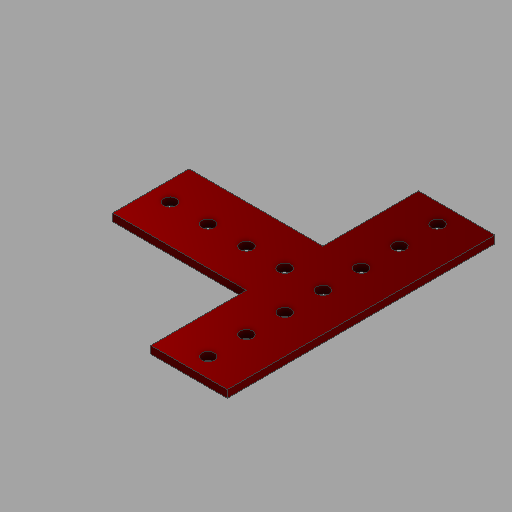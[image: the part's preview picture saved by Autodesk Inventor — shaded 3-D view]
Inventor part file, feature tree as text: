
AUTODESK INVENTOR PART (.ipt)
format: ipt  version: 2024.2 (Build 282272000, 272)  size: 332,800 bytes
history: native  units: in
note: dims shown in document units (in); Inventor stores cm internally (conversion verified against a paired STEP export)
features: extrude x1, sketch x1, projected_geometry x1
ambient origin geometry x8: Origin, YZ Plane, XZ Plane, XY Plane, X Axis, Y Axis, Z Axis, Center Point
bodies: Solid2 (feature_tree), Solid1 (feature_tree)
feature tree (3):
  extrude  "Extrusion1"  Depth=0.375in TaperAngle=0.0deg
  sketch  "Sketch1"  dims[d0=0.5in d1=0.375in d2=0.0in]
  projected_geometry  "Projected Loop1"
